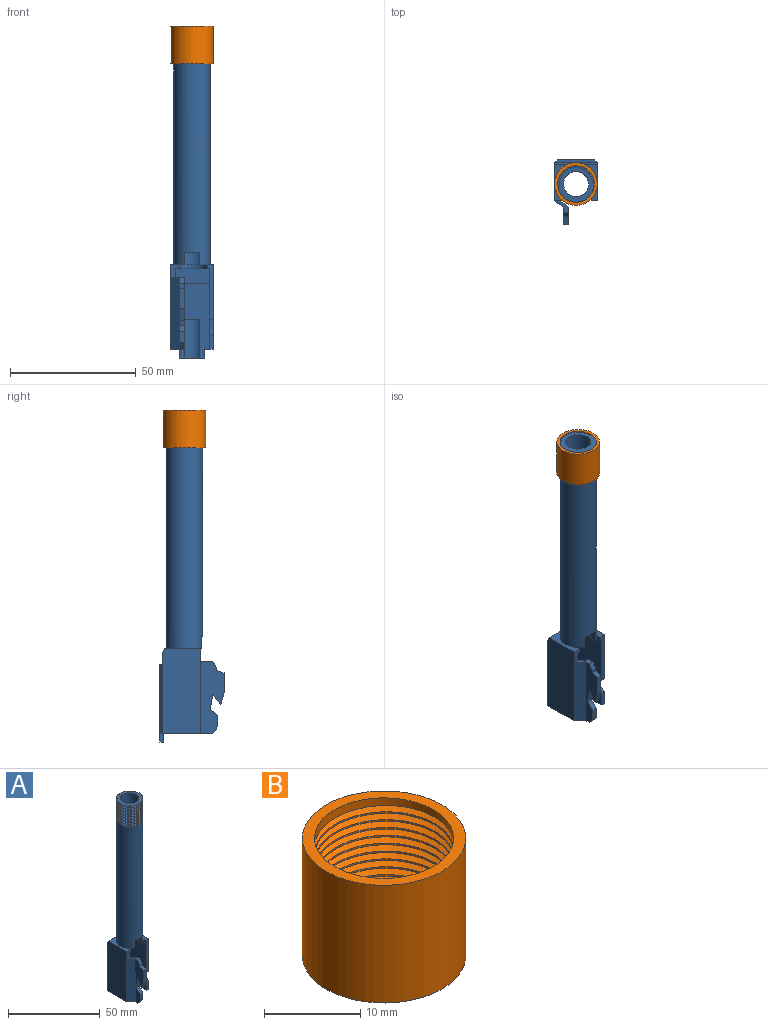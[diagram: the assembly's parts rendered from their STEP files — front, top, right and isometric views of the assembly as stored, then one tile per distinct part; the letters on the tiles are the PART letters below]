
ASSEMBLY  parts=2 mates=1
PART A: 71 faces, bbox 17.5x26x132.9 mm
  f0: cylinder r=7.25mm len=82.2mm, axis (0,0,-1), area 3668.9mm2, adj f13,f20,f23,f51,f52,f53,f68,f69
  f1: cylinder r=7.25mm len=14.5mm, axis (0,0,-1), area 11.8mm2, adj f2,f29,f67,f69,f70
  f2: cylinder r=7.25mm len=14.5mm, axis (0,0,-1), area 9.1mm2, adj f1,f3,f69,f70
  f3: cylinder r=7.25mm len=14.5mm, axis (0,0,-1), area 9.1mm2, adj f2,f4,f69,f70
  f4: cylinder r=7.25mm len=14.5mm, axis (0,0,-1), area 9.1mm2, adj f3,f5,f69,f70
  f5: cylinder r=7.25mm len=14.5mm, axis (0,0,-1), area 9.1mm2, adj f4,f6,f69,f70
  f6: cylinder r=7.25mm len=14.5mm, axis (0,0,-1), area 9.1mm2, adj f5,f7,f69,f70
  f7: cylinder r=7.25mm len=14.5mm, axis (0,0,-1), area 9.1mm2, adj f6,f8,f69,f70
  f8: cylinder r=7.25mm len=14.5mm, axis (0,0,-1), area 9.1mm2, adj f7,f9,f69,f70
  f9: cylinder r=7.25mm len=14.5mm, axis (0,0,-1), area 9.1mm2, adj f8,f10,f69,f70
  f10: cylinder r=7.25mm len=14.5mm, axis (0,0,-1), area 9.1mm2, adj f9,f11,f69,f70
  f11: cylinder r=7.25mm len=14.5mm, axis (0,0,-1), area 9.1mm2, adj f10,f12,f69,f70
  f12: cylinder r=7.25mm len=14.5mm, axis (0,0,-1), area 9.1mm2, adj f11,f13,f69,f70
  f13: cylinder r=7.25mm len=14.5mm, axis (0,0,-1), area 9.1mm2, adj f0,f12,f69,f70
  f14: plane 21.5x2.5mm, normal (0,-1,0), area 33.8mm2, adj f18,f23,f31,f40,f50,f66
  f15: plane 21x5.5mm, normal (0,0,-1), area 43.8mm2, adj f26,f30,f34,f37,f41,f42,f45,f46
  f16: plane 8x2mm, normal (0,-1,0), area 16mm2, adj f46,f47,f56,f58
  f17: plane 5.5x5mm, normal (0,0,1), area 10mm2, adj f22,f45,f46,f47,f48,f55
  f18: plane 13.5x13.5mm, normal (0,0,-1), area 53.1mm2, adj f14,f19,f22,f40,f41,f44,f49,f50
  f19: cylinder r=6mm len=12mm, axis (0,0,1), area 32.9mm2, adj f18,f20,f49,f54
  f20: plane 12.6x12mm, normal (0,0,-1), area 38.1mm2, adj f0,f19,f21,f49,f52,f53,f54
  f21: cylinder r=5mm len=95mm, axis (0,0,-1), area 2952.3mm2, adj f20,f29,f51,f52,f53
  f22: plane 5x3mm, normal (0,-1,0), area 11.5mm2, adj f17,f18,f23,f30,f41,f49
  f23: plane 17x14mm, normal (0,0,1), area 74.4mm2, adj f0,f14,f22,f30,f31,f32,f49,f50
  f24: plane 13.5x1mm, normal (0,0,-1), area 13.5mm2, adj f37,f40,f41,f44
  f25: plane 6x1.5mm, normal (0,-1,0), area 9mm2, adj f28,f31,f40,f64
  f26: plane 31x15mm, normal (0,1,0), area 447.5mm2, adj f15,f27,f28,f34,f35,f36,f42,f43
  f27: plane 17x1mm, normal (0,0,1), area 16mm2, adj f26,f33,f42,f43
  f28: plane 16x3.5mm, normal (0,0,-1), area 26.5mm2, adj f25,f26,f31,f35,f37,f40,f43
  f29: plane 15x14.75mm, normal (0,0,1), area 80.5mm2, adj f1,f21,f67,f70
  f30: plane 33.5x15mm, normal (-1,0,0), area 501.5mm2, adj f15,f22,f23,f32,f33,f42,f48
  f31: plane 33.5x15mm, normal (1,0,0), area 486.5mm2, adj f14,f23,f25,f28,f32,f33,f43,f64
  f32: plane 17x2mm, normal (0,0.89,0.45), area 38mm2, adj f23,f30,f31,f33
  f33: plane 17x4mm, normal (0,1,0), area 68mm2, adj f27,f30,f31,f32
  f34: plane 3.5x1.5mm, normal (-1,0,0), area 5.2mm2, adj f15,f26,f36,f37
  f35: plane 3.5x1.5mm, normal (1,0,0), area 5.2mm2, adj f26,f28,f36,f37
  f36: plane 10x1.5mm, normal (0,0,-1), area 10.9mm2, adj f26,f34,f35,f37,f38
  f37: plane 29.5x13.5mm, normal (0,-1,0), area 293mm2, adj f15,f24,f28,f34,f35,f36,f38,f39
  f38: cylinder r=5mm len=15.5mm, axis (0,0,-1), area 99.7mm2, adj f36,f37,f39
  f39: plane 6x1mm, normal (0,0,-1), area 4.1mm2, adj f37,f38
  f40: plane 32x14.5mm, normal (-1,0,0), area 443mm2, adj f14,f18,f24,f25,f28,f37,f44,f64
  f41: plane 32x14.5mm, normal (1,0,0), area 458mm2, adj f15,f18,f22,f24,f37,f44,f45
  f42: plane 27.5x1mm, normal (-0.71,0.71,0), area 38.9mm2, adj f15,f26,f27,f30
  f43: plane 27.5x1mm, normal (0.71,0.71,0), area 38.9mm2, adj f26,f27,f28,f31
  f44: plane 13.5x6mm, normal (0,-1,0), area 81mm2, adj f18,f24,f40,f41
  f45: plane 28.5x3.5mm, normal (0.65,0.76,0), area 131.4mm2, adj f15,f17,f41,f46
  f46: plane 28.5x6.5mm, normal (1,0,0), area 120mm2, adj f15,f16,f17,f45,f55,f56,f57,f58
  f47: plane 28.5x6.5mm, normal (-1,0,0), area 120mm2, adj f15,f16,f17,f48,f55,f56,f57,f58
  f48: plane 28.5x3.5mm, normal (-0.65,-0.76,0), area 131.4mm2, adj f15,f17,f30,f47
  f49: plane 3.85x1.5mm, normal (1,0,0), area 5.8mm2, adj f18,f19,f20,f22,f23
  f50: plane 2.18x1.5mm, normal (-1,0,0), area 3.3mm2, adj f14,f18,f23,f54
  f51: plane 6x3.25mm, normal (0,0,-1), area 14.1mm2, adj f0,f21,f52,f53
  f52: plane 5x2.6mm, normal (1,0,0), area 13mm2, adj f0,f20,f21,f51
  f53: plane 5x2.6mm, normal (-1,0,0), area 13mm2, adj f0,f20,f21,f51
  f54: plane 3.44x1.5mm, normal (-1,-0.01,0), area 5.2mm2, adj f18,f19,f20,f50
  f55: plane 2.5x2mm, normal (0,-0.86,0.51), area 5.8mm2, adj f17,f46,f47,f57
  f56: plane 3x2mm, normal (0,-0.32,0.95), area 6.3mm2, adj f16,f46,f47,f57
  f57: plane 2x1mm, normal (0,-1,0), area 2mm2, adj f46,f47,f55,f56
  f58: plane 4.5x2mm, normal (0,-0.96,-0.28), area 9.4mm2, adj f16,f46,f47,f60
  f59: plane 2.5x2mm, normal (0,-0.78,-0.62), area 6.4mm2, adj f15,f46,f47,f63
  f60: plane 4x3.2mm, normal (0,0.78,-0.62), area 10.2mm2, adj f46,f47,f58,f61
  f61: plane 6x2mm, normal (0,-0.99,-0.16), area 12.2mm2, adj f46,f47,f60,f62
  f62: plane 3x2.5mm, normal (0,-0.64,0.77), area 7.8mm2, adj f46,f47,f61,f63
  f63: plane 4.5x2mm, normal (0,-1,0), area 9mm2, adj f46,f47,f59,f62
  f64: plane 3x2mm, normal (0,-0.55,0.83), area 5.4mm2, adj f25,f31,f40,f65
  f65: plane 4x1.5mm, normal (0,-1,0), area 6mm2, adj f31,f40,f64,f66
  f66: plane 3x1.5mm, normal (0,0,-1), area 4.5mm2, adj f14,f31,f40,f65
  f67: plane 0.69x0.4mm, normal (0,1,0), area 0.1mm2, adj f1,f29,f69
  f68: plane 0.8x0.69mm, normal (0,-1,0), area 0.3mm2, adj f0,f69,f70
  f69: bspline ~16.74x14.5mm, area 488.8mm2, adj f0,f1,f2,f3,f4,f5,f6,f7
  f70: bspline ~16.74x14.5mm, area 478.8mm2, adj f0,f1,f2,f3,f4,f5,f6,f7
PART B: 21 faces, bbox 18.8x17.5x15.9 mm
  f0: plane 17.48x17.48mm, normal (0,0,-1), area 55.3mm2, adj f1,f15,f17,f18
  f1: cylinder r=7.25mm len=14.5mm, axis (0,0,-1), area 11.8mm2, adj f0,f2,f17,f18,f20
  f2: cylinder r=7.25mm len=14.5mm, axis (0,0,-1), area 9.1mm2, adj f1,f3,f18,f20
  f3: cylinder r=7.25mm len=14.5mm, axis (0,0,-1), area 9.1mm2, adj f2,f4,f18,f20
  f4: cylinder r=7.25mm len=14.5mm, axis (0,0,-1), area 9.1mm2, adj f3,f5,f18,f20
  f5: cylinder r=7.25mm len=14.5mm, axis (0,0,-1), area 9.1mm2, adj f4,f6,f18,f20
  f6: cylinder r=7.25mm len=14.5mm, axis (0,0,-1), area 9.1mm2, adj f5,f7,f18,f20
  f7: cylinder r=7.25mm len=14.5mm, axis (0,0,-1), area 9.1mm2, adj f6,f8,f18,f20
  f8: cylinder r=7.25mm len=14.5mm, axis (0,0,-1), area 9.1mm2, adj f7,f9,f18,f20
  f9: cylinder r=7.25mm len=14.5mm, axis (0,0,-1), area 9.1mm2, adj f8,f10,f18,f20
  f10: cylinder r=7.25mm len=14.5mm, axis (0,0,-1), area 9.1mm2, adj f9,f11,f18,f20
  f11: cylinder r=7.25mm len=14.5mm, axis (0,0,-1), area 9.1mm2, adj f10,f12,f18,f20
  f12: cylinder r=7.25mm len=14.5mm, axis (0,0,-1), area 9.1mm2, adj f11,f13,f18,f20
  f13: cylinder r=7.25mm len=14.5mm, axis (0,0,-1), area 9.1mm2, adj f12,f14,f18,f20
  f14: cylinder r=7.25mm len=14.5mm, axis (0,0,-1), area 55.6mm2, adj f13,f16,f18,f19,f20
  f15: cylinder r=8.5mm len=17mm, axis (0,0,-1), area 801.1mm2, adj f0,f16
  f16: plane 17x17mm, normal (0,0,1), area 61.9mm2, adj f14,f15
  f17: plane 0.69x0.4mm, normal (-1,0,0), area 0.1mm2, adj f0,f1,f20
  f18: bspline ~18.34x15.89mm, area 530.3mm2, adj f0,f1,f2,f3,f4,f5,f6,f7
  f19: plane 0.8x0.69mm, normal (1,0,0), area 0.3mm2, adj f14,f18,f20
  f20: bspline ~18.34x15.89mm, area 534.6mm2, adj f1,f2,f3,f4,f5,f6,f7,f8
PLACE A t=(-49.16,-0.23,-45.27)mm
PLACE B t=(-49.16,-0.23,34.73)mm
MATE revolute A.f0 <-> B.f1  axis (0,0,1) through (-49.16,-0.23,49.73)mm
